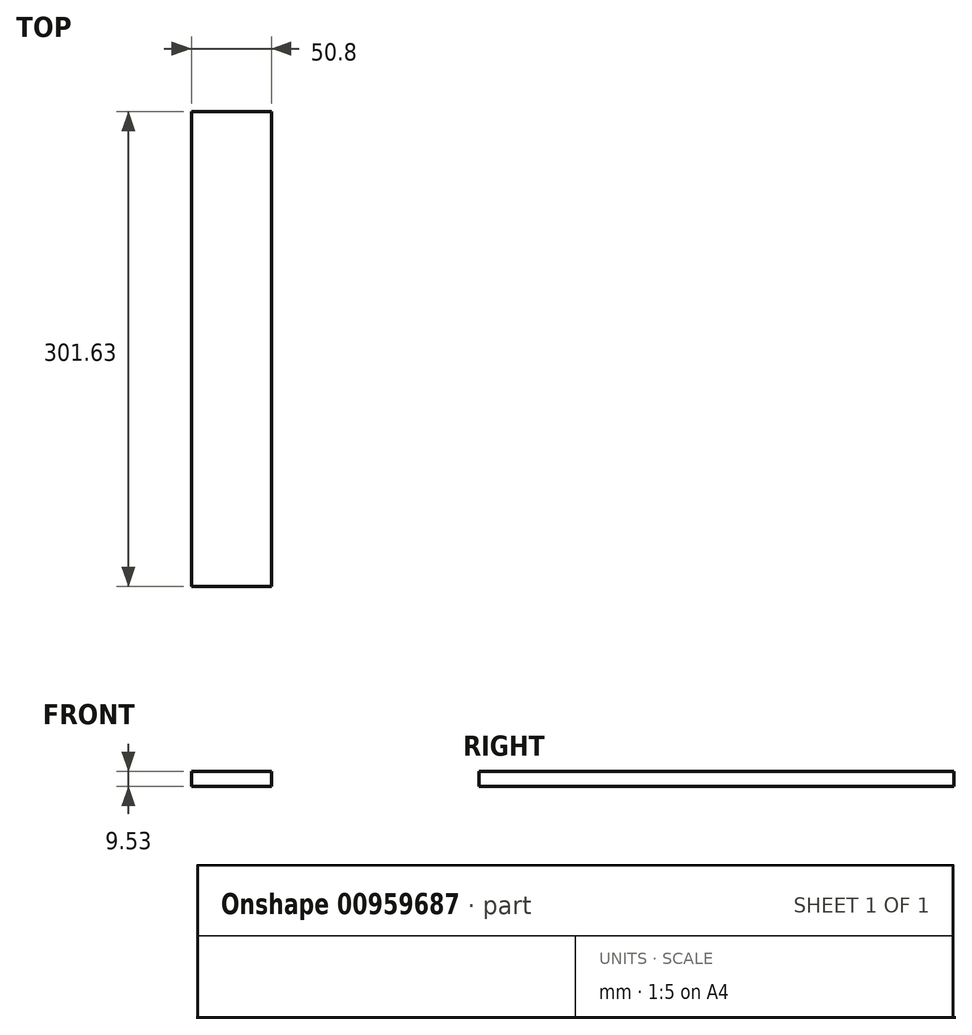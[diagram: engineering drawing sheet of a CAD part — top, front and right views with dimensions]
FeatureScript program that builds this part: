
annotation { "Feature Type Name" : "Feature", "Feature Type Description" : "" }
export const myFeature = defineFeature(function(context is Context, id is Id, definition is map)
    precondition{}
    {
        {
            var Q0;
            Q0=qCreatedBy(makeId("Top.planeOp"),FACE);
            var sketch = newSketch(context, id + "F0", { "sketchPlane" : qUnion([Q0])});
            skLineSegment(sketch, "E0.bottom", {"start": v(-1799.8, 122.92) * mm, "end": v(-1749, 122.92) * mm});
            skLineSegment(sketch, "E0.top", {"start": v(-1799.8, -178.7) * mm, "end": v(-1749, -178.7) * mm});
            skLineSegment(sketch, "E0.left", {"start": v(-1799.8, 122.92) * mm, "end": v(-1799.8, -178.7) * mm});
            skLineSegment(sketch, "E0.right", {"start": v(-1749, 122.92) * mm, "end": v(-1749, -178.7) * mm});
            skSolve(sketch);
        }
        {
            var Q0;
            Q0=makeQuery(id+"F0.imprint","IMPRINT",FACE,{"disambiguationData":[TD([[makeQuery(id+"F0.imprint","IMPRINT",EDGE,{"derivedFrom":sQuery(id+"F0.wireOp",EDGE,"E0.bottom")}),-1.0]])]});
            extrude(context, id + "F1", {"entities" : qUnion([Q0]), "depth" : 9.52 * mm, "offsetDistance" : 25.4 * mm});
        }
    });
